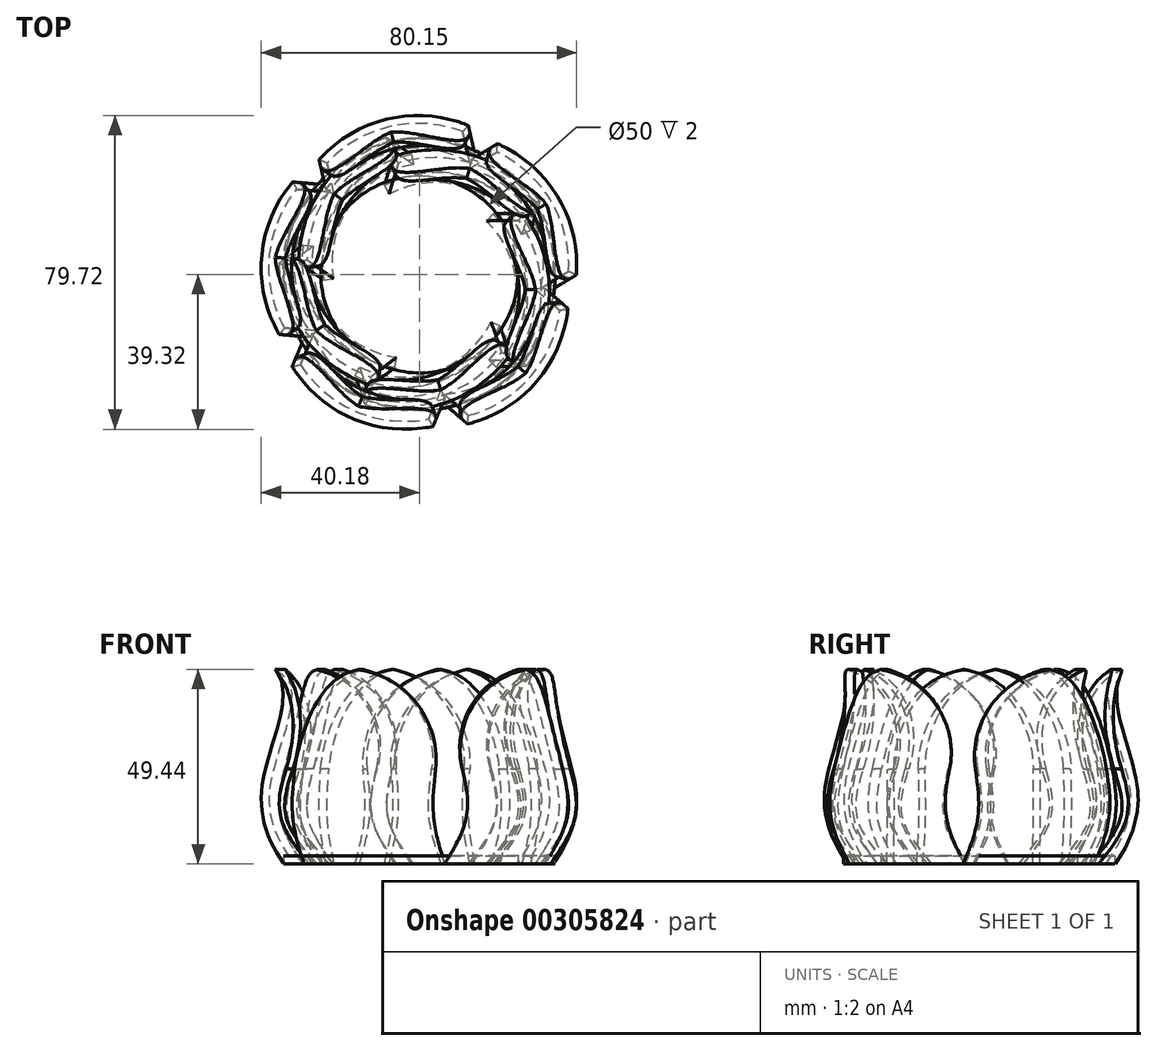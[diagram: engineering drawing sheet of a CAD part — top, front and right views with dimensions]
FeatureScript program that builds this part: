
annotation { "Feature Type Name" : "Feature", "Feature Type Description" : "" }
export const myFeature = defineFeature(function(context is Context, id is Id, definition is map)
    precondition{}
    {
        {
            var Q0;
            Q0=qCreatedBy(makeId("Top.planeOp"),FACE);
            var sketch = newSketch(context, id + "F0", { "sketchPlane" : qUnion([Q0])});
            skCircle(sketch, "E0", {"center": v(0, 0) * mm, "radius": 25 * mm});
            skSolve(sketch);
        }
        {
            var Q0;
            Q0=makeQuery(id+"F0.imprint","IMPRINT",FACE,{"disambiguationData":[TD([[makeQuery(id+"F0.imprint","IMPRINT",EDGE,{"derivedFrom":sQuery(id+"F0.wireOp",EDGE,"E0")}),1.0]])]});
            extrude(context, id + "F1", {"entities" : qUnion([Q0]), "depth" : 2 * mm});
        }
        {
            var Q0;
            Q0=qCreatedBy(makeId("Top.planeOp"),FACE);
            var sketch = newSketch(context, id + "F2", { "sketchPlane" : qUnion([Q0])});
            skArc(sketch, "E1.0", {"start": v(0, 25) * mm, "mid": v(-17.68, 17.68) * mm, "end": v(-25, 0) * mm});
            skArc(sketch, "E2.0", {"start": v(0, 27.5) * mm, "mid": v(-19.45, 19.45) * mm, "end": v(-27.5, 0) * mm});
            skLineSegment(sketch, "E3", {"start": v(0, 27.5) * mm, "end": v(0, 25) * mm});
            skLineSegment(sketch, "E4", {"start": v(-27.5, 0) * mm, "end": v(-25, 0) * mm});
            skSolve(sketch);
        }
        {
            var Q0;
            Q0=qCreatedBy(makeId("Right.planeOp"),FACE);
            var Q1;
            Q1=qCreatedBy(makeId("Front.planeOp"),FACE);
            cPlane(context, id + "F3", {"entities" : qUnion([Q0, Q1]), "cplaneType" : CPlaneType.MID_PLANE, "offset" : 25 * mm, "width" : 150 * mm, "height" : 150 * mm});
        }
        {
            var Q0;
            Q0=qCreatedBy(id+"F3.planeOp",FACE);
            var sketch = newSketch(context, id + "F4", { "sketchPlane" : qUnion([Q0])});
            skLineSegment(sketch, "E5.0", {"start": v(19.45, 0) * mm, "end": v(27.5, 0) * mm});
            skFitSpline(sketch, "E6", {"points": [v(27.5, 0) * mm, v(32.88, 21.22) * mm, v(30.27, 49.8) * mm], "startDerivative": vector(27.76, 40.4) * mm, "endDerivative": vector(35.36, 33.4) * mm});
            skSolve(sketch);
        }
        {
            var Q0;
            Q0=makeQuery(id+"F2.imprint","IMPRINT",FACE,{"disambiguationData":[TD([[makeQuery(id+"F2.imprint","IMPRINT",EDGE,{"derivedFrom":sQuery(id+"F2.wireOp",EDGE,"E1.0")}),-1.0]])]});
            var Q1;
            Q1=sQuery(id+"F4.wireOp",EDGE,"E6");
            sweep(context, id + "F5", {"profiles" : qUnion([Q0]), "path" : qUnion([Q1])});
        }
        {
            var Q0;
            Q0=qCreatedBy(id+"F3.planeOp",FACE);
            var sketch = newSketch(context, id + "F6", { "sketchPlane" : qUnion([Q0])});
            skLineSegment(sketch, "E7.0", {"start": v(-25, 2) * mm, "end": v(25, 2) * mm});
            skLineSegment(sketch, "E8", {"start": v(25, 2) * mm, "end": v(25, 51.54) * mm, "construction": true});
            skSolve(sketch);
        }
        {
            var Q0;
            Q0=makeQuery(id+"F5.opSweep","SWEPT_BODY",BODY,{"disambiguationData":[OSD([sQuery(id+"F2.wireOp",EDGE,"E1.0"),sQuery(id+"F2.wireOp",EDGE,"E2.0"),sQuery(id+"F2.wireOp",EDGE,"E3"),sQuery(id+"F2.wireOp",EDGE,"E4"),sQuery(id+"F4.wireOp",EDGE,"E6")])]});
            var Q1;
            Q1=sQuery(id+"F6.wireOp",EDGE,"E8");
            transform(context, id + "F7", {"entities" : qUnion([Q0]), "transformType" : TransformType.ROTATION, "transformAxis" : qUnion([Q1]), "angle" : 10 * degree, "makeCopy" : false});
        }
        {
            var Q0;
            Q0=makeQuery(id+"F5.opSweep","SWEPT_BODY",BODY,{"disambiguationData":[OSD([sQuery(id+"F2.wireOp",EDGE,"E1.0"),sQuery(id+"F2.wireOp",EDGE,"E2.0"),sQuery(id+"F2.wireOp",EDGE,"E3"),sQuery(id+"F2.wireOp",EDGE,"E4"),sQuery(id+"F4.wireOp",EDGE,"E6")])]});
            var Q1;
            Q1=makeQuery(id+"F1.opExtrude","CAP_EDGE",EDGE,{"disambiguationData":[OSD([sQuery(id+"F0.wireOp",EDGE,"E0")])],"isStart":false});
            circularPattern(context, id + "F8", {"entities" : qUnion([Q0]), "axis" : qUnion([Q1]), "angle" : 360 * degree, "instanceCount" : 5, "equalSpace" : true});
        }
        {
            var Q0;
            Q0=makeQuery(id+"F8.opPattern","COPY",BODY,{"derivedFrom":makeQuery(id+"F5.opSweep","SWEPT_BODY",BODY,{"disambiguationData":[OSD([sQuery(id+"F2.wireOp",EDGE,"E1.0"),sQuery(id+"F2.wireOp",EDGE,"E2.0"),sQuery(id+"F2.wireOp",EDGE,"E3"),sQuery(id+"F2.wireOp",EDGE,"E4"),sQuery(id+"F4.wireOp",EDGE,"E6")])]}),"instanceName":"4"});
            transform(context, id + "F9", {"entities" : qUnion([Q0]), "transformType" : TransformType.COPY});
        }
        {
            var Q0;
            Q0=makeQuery(id+"F9.opPattern","COPY",BODY,{"derivedFrom":makeQuery(id+"F8.opPattern","COPY",BODY,{"derivedFrom":makeQuery(id+"F5.opSweep","SWEPT_BODY",BODY,{"disambiguationData":[OSD([sQuery(id+"F2.wireOp",EDGE,"E1.0"),sQuery(id+"F2.wireOp",EDGE,"E2.0"),sQuery(id+"F2.wireOp",EDGE,"E3"),sQuery(id+"F2.wireOp",EDGE,"E4"),sQuery(id+"F4.wireOp",EDGE,"E6")])]}),"instanceName":"4"}),"instanceName":"1"});
            transform(context, id + "F10", {"entities" : qUnion([Q0]), "transformType" : TransformType.TRANSLATION_3D, "dx" : -14.4 * mm, "dy" : 8.9 * mm, "dz" : 0 * mm, "makeCopy" : false});
        }
        {
            var Q0;
            Q0=qCreatedBy(makeId("Right.planeOp"),FACE);
            var sketch = newSketch(context, id + "F11", { "sketchPlane" : qUnion([Q0])});
            skLineSegment(sketch, "E9", {"start": v(24.37, 0) * mm, "end": v(24.37, 62.17) * mm, "construction": true});
            skSolve(sketch);
        }
        {
            var Q0;
            Q0=makeQuery(id+"F9.opPattern","COPY",BODY,{"derivedFrom":makeQuery(id+"F8.opPattern","COPY",BODY,{"derivedFrom":makeQuery(id+"F5.opSweep","SWEPT_BODY",BODY,{"disambiguationData":[OSD([sQuery(id+"F2.wireOp",EDGE,"E1.0"),sQuery(id+"F2.wireOp",EDGE,"E2.0"),sQuery(id+"F2.wireOp",EDGE,"E3"),sQuery(id+"F2.wireOp",EDGE,"E4"),sQuery(id+"F4.wireOp",EDGE,"E6")])]}),"instanceName":"4"}),"instanceName":"1"});
            var Q1;
            Q1=sQuery(id+"F11.wireOp",EDGE,"E9");
            transform(context, id + "F12", {"entities" : qUnion([Q0]), "transformType" : TransformType.ROTATION, "transformAxis" : qUnion([Q1]), "angle" : 30 * degree, "makeCopy" : false});
        }
        {
            var Q0;
            Q0=makeQuery(id+"F9.opPattern","COPY",BODY,{"derivedFrom":makeQuery(id+"F8.opPattern","COPY",BODY,{"derivedFrom":makeQuery(id+"F5.opSweep","SWEPT_BODY",BODY,{"disambiguationData":[OSD([sQuery(id+"F2.wireOp",EDGE,"E1.0"),sQuery(id+"F2.wireOp",EDGE,"E2.0"),sQuery(id+"F2.wireOp",EDGE,"E3"),sQuery(id+"F2.wireOp",EDGE,"E4"),sQuery(id+"F4.wireOp",EDGE,"E6")])]}),"instanceName":"4"}),"instanceName":"1"});
            transform(context, id + "F13", {"entities" : qUnion([Q0]), "transformType" : TransformType.TRANSLATION_3D, "dx" : 0 * mm, "dy" : 2.7 * mm, "dz" : 0 * mm, "makeCopy" : false});
        }
        {
            var Q0;
            Q0=makeQuery(id+"F9.opPattern","COPY",BODY,{"derivedFrom":makeQuery(id+"F8.opPattern","COPY",BODY,{"derivedFrom":makeQuery(id+"F5.opSweep","SWEPT_BODY",BODY,{"disambiguationData":[OSD([sQuery(id+"F2.wireOp",EDGE,"E1.0"),sQuery(id+"F2.wireOp",EDGE,"E2.0"),sQuery(id+"F2.wireOp",EDGE,"E3"),sQuery(id+"F2.wireOp",EDGE,"E4"),sQuery(id+"F4.wireOp",EDGE,"E6")])]}),"instanceName":"4"}),"instanceName":"1"});
            var Q1;
            Q1=makeQuery(id+"F1.opExtrude","CAP_EDGE",EDGE,{"disambiguationData":[OSD([sQuery(id+"F0.wireOp",EDGE,"E0")])],"isStart":false});
            circularPattern(context, id + "F14", {"entities" : qUnion([Q0]), "axis" : qUnion([Q1]), "angle" : 360 * degree, "instanceCount" : 5, "equalSpace" : true});
        }
        {
            var Q0;
            Q0=makeQuery(id+"F8.opPattern","COPY",EDGE,{"derivedFrom":makeQuery(id+"F5.opSweep","CAP_EDGE",EDGE,{"disambiguationData":[OSD([sQuery(id+"F2.wireOp",EDGE,"E4"),sQuery(id+"F4.wireOp",VERTEX,"E6.end")])],"isStart":false}),"instanceName":"1"});
            var Q1;
            Q1=makeQuery(id+"F8.opPattern","COPY",EDGE,{"derivedFrom":makeQuery(id+"F5.opSweep","CAP_EDGE",EDGE,{"disambiguationData":[OSD([sQuery(id+"F2.wireOp",EDGE,"E3"),sQuery(id+"F4.wireOp",VERTEX,"E6.end")])],"isStart":false}),"instanceName":"1"});
            var Q2;
            Q2=makeQuery(id+"F5.opSweep","CAP_EDGE",EDGE,{"disambiguationData":[OSD([sQuery(id+"F2.wireOp",EDGE,"E4"),sQuery(id+"F4.wireOp",VERTEX,"E6.end")])],"isStart":false});
            var Q3;
            Q3=makeQuery(id+"F5.opSweep","CAP_EDGE",EDGE,{"disambiguationData":[OSD([sQuery(id+"F2.wireOp",EDGE,"E3"),sQuery(id+"F4.wireOp",VERTEX,"E6.end")])],"isStart":false});
            var Q4;
            Q4=makeQuery(id+"F8.opPattern","COPY",EDGE,{"derivedFrom":makeQuery(id+"F5.opSweep","CAP_EDGE",EDGE,{"disambiguationData":[OSD([sQuery(id+"F2.wireOp",EDGE,"E4"),sQuery(id+"F4.wireOp",VERTEX,"E6.end")])],"isStart":false}),"instanceName":"4"});
            var Q5;
            Q5=makeQuery(id+"F9.opPattern","COPY",EDGE,{"derivedFrom":makeQuery(id+"F8.opPattern","COPY",EDGE,{"derivedFrom":makeQuery(id+"F5.opSweep","CAP_EDGE",EDGE,{"disambiguationData":[OSD([sQuery(id+"F2.wireOp",EDGE,"E4"),sQuery(id+"F4.wireOp",VERTEX,"E6.end")])],"isStart":false}),"instanceName":"4"}),"instanceName":"1"});
            var Q6;
            Q6=makeQuery(id+"F14.opPattern","COPY",EDGE,{"derivedFrom":makeQuery(id+"F9.opPattern","COPY",EDGE,{"derivedFrom":makeQuery(id+"F8.opPattern","COPY",EDGE,{"derivedFrom":makeQuery(id+"F5.opSweep","CAP_EDGE",EDGE,{"disambiguationData":[OSD([sQuery(id+"F2.wireOp",EDGE,"E3"),sQuery(id+"F4.wireOp",VERTEX,"E6.end")])],"isStart":false}),"instanceName":"4"}),"instanceName":"1"}),"instanceName":"1"});
            var Q7;
            Q7=makeQuery(id+"F9.opPattern","COPY",EDGE,{"derivedFrom":makeQuery(id+"F8.opPattern","COPY",EDGE,{"derivedFrom":makeQuery(id+"F5.opSweep","CAP_EDGE",EDGE,{"disambiguationData":[OSD([sQuery(id+"F2.wireOp",EDGE,"E3"),sQuery(id+"F4.wireOp",VERTEX,"E6.end")])],"isStart":false}),"instanceName":"4"}),"instanceName":"1"});
            var Q8;
            Q8=makeQuery(id+"F14.opPattern","COPY",EDGE,{"derivedFrom":makeQuery(id+"F9.opPattern","COPY",EDGE,{"derivedFrom":makeQuery(id+"F8.opPattern","COPY",EDGE,{"derivedFrom":makeQuery(id+"F5.opSweep","CAP_EDGE",EDGE,{"disambiguationData":[OSD([sQuery(id+"F2.wireOp",EDGE,"E4"),sQuery(id+"F4.wireOp",VERTEX,"E6.end")])],"isStart":false}),"instanceName":"4"}),"instanceName":"1"}),"instanceName":"4"});
            var Q9;
            Q9=makeQuery(id+"F8.opPattern","COPY",EDGE,{"derivedFrom":makeQuery(id+"F5.opSweep","CAP_EDGE",EDGE,{"disambiguationData":[OSD([sQuery(id+"F2.wireOp",EDGE,"E3"),sQuery(id+"F4.wireOp",VERTEX,"E6.end")])],"isStart":false}),"instanceName":"4"});
            var Q10;
            Q10=makeQuery(id+"F8.opPattern","COPY",EDGE,{"derivedFrom":makeQuery(id+"F5.opSweep","CAP_EDGE",EDGE,{"disambiguationData":[OSD([sQuery(id+"F2.wireOp",EDGE,"E4"),sQuery(id+"F4.wireOp",VERTEX,"E6.end")])],"isStart":false}),"instanceName":"3"});
            var Q11;
            Q11=makeQuery(id+"F14.opPattern","COPY",EDGE,{"derivedFrom":makeQuery(id+"F9.opPattern","COPY",EDGE,{"derivedFrom":makeQuery(id+"F8.opPattern","COPY",EDGE,{"derivedFrom":makeQuery(id+"F5.opSweep","CAP_EDGE",EDGE,{"disambiguationData":[OSD([sQuery(id+"F2.wireOp",EDGE,"E3"),sQuery(id+"F4.wireOp",VERTEX,"E6.end")])],"isStart":false}),"instanceName":"4"}),"instanceName":"1"}),"instanceName":"4"});
            var Q12;
            Q12=makeQuery(id+"F14.opPattern","COPY",EDGE,{"derivedFrom":makeQuery(id+"F9.opPattern","COPY",EDGE,{"derivedFrom":makeQuery(id+"F8.opPattern","COPY",EDGE,{"derivedFrom":makeQuery(id+"F5.opSweep","CAP_EDGE",EDGE,{"disambiguationData":[OSD([sQuery(id+"F2.wireOp",EDGE,"E4"),sQuery(id+"F4.wireOp",VERTEX,"E6.end")])],"isStart":false}),"instanceName":"4"}),"instanceName":"1"}),"instanceName":"3"});
            var Q13;
            Q13=makeQuery(id+"F8.opPattern","COPY",EDGE,{"derivedFrom":makeQuery(id+"F5.opSweep","CAP_EDGE",EDGE,{"disambiguationData":[OSD([sQuery(id+"F2.wireOp",EDGE,"E3"),sQuery(id+"F4.wireOp",VERTEX,"E6.end")])],"isStart":false}),"instanceName":"3"});
            var Q14;
            Q14=makeQuery(id+"F8.opPattern","COPY",EDGE,{"derivedFrom":makeQuery(id+"F5.opSweep","CAP_EDGE",EDGE,{"disambiguationData":[OSD([sQuery(id+"F2.wireOp",EDGE,"E4"),sQuery(id+"F4.wireOp",VERTEX,"E6.end")])],"isStart":false}),"instanceName":"2"});
            var Q15;
            Q15=makeQuery(id+"F14.opPattern","COPY",EDGE,{"derivedFrom":makeQuery(id+"F9.opPattern","COPY",EDGE,{"derivedFrom":makeQuery(id+"F8.opPattern","COPY",EDGE,{"derivedFrom":makeQuery(id+"F5.opSweep","CAP_EDGE",EDGE,{"disambiguationData":[OSD([sQuery(id+"F2.wireOp",EDGE,"E3"),sQuery(id+"F4.wireOp",VERTEX,"E6.end")])],"isStart":false}),"instanceName":"4"}),"instanceName":"1"}),"instanceName":"3"});
            var Q16;
            Q16=makeQuery(id+"F14.opPattern","COPY",EDGE,{"derivedFrom":makeQuery(id+"F9.opPattern","COPY",EDGE,{"derivedFrom":makeQuery(id+"F8.opPattern","COPY",EDGE,{"derivedFrom":makeQuery(id+"F5.opSweep","CAP_EDGE",EDGE,{"disambiguationData":[OSD([sQuery(id+"F2.wireOp",EDGE,"E4"),sQuery(id+"F4.wireOp",VERTEX,"E6.end")])],"isStart":false}),"instanceName":"4"}),"instanceName":"1"}),"instanceName":"2"});
            var Q17;
            Q17=makeQuery(id+"F8.opPattern","COPY",EDGE,{"derivedFrom":makeQuery(id+"F5.opSweep","CAP_EDGE",EDGE,{"disambiguationData":[OSD([sQuery(id+"F2.wireOp",EDGE,"E3"),sQuery(id+"F4.wireOp",VERTEX,"E6.end")])],"isStart":false}),"instanceName":"2"});
            var Q18;
            Q18=makeQuery(id+"F14.opPattern","COPY",EDGE,{"derivedFrom":makeQuery(id+"F9.opPattern","COPY",EDGE,{"derivedFrom":makeQuery(id+"F8.opPattern","COPY",EDGE,{"derivedFrom":makeQuery(id+"F5.opSweep","CAP_EDGE",EDGE,{"disambiguationData":[OSD([sQuery(id+"F2.wireOp",EDGE,"E3"),sQuery(id+"F4.wireOp",VERTEX,"E6.end")])],"isStart":false}),"instanceName":"4"}),"instanceName":"1"}),"instanceName":"2"});
            var Q19;
            Q19=makeQuery(id+"F14.opPattern","COPY",EDGE,{"derivedFrom":makeQuery(id+"F9.opPattern","COPY",EDGE,{"derivedFrom":makeQuery(id+"F8.opPattern","COPY",EDGE,{"derivedFrom":makeQuery(id+"F5.opSweep","CAP_EDGE",EDGE,{"disambiguationData":[OSD([sQuery(id+"F2.wireOp",EDGE,"E4"),sQuery(id+"F4.wireOp",VERTEX,"E6.end")])],"isStart":false}),"instanceName":"4"}),"instanceName":"1"}),"instanceName":"1"});
            fillet(context, id + "F15", {"entities" : qUnion([Q0, Q1, Q2, Q3, Q4, Q5, Q6, Q7, Q8, Q9, Q10, Q11, Q12, Q13, Q14, Q15, Q16, Q17, Q18, Q19]), "radius" : 19 * mm, "tangentPropagation" : true, "allowEdgeOverflow" : false});
        }
        {
            var Q0;
            Q0=qCreatedBy(makeId("Top.planeOp"),FACE);
            var sketch = newSketch(context, id + "F16", { "sketchPlane" : qUnion([Q0])});
            skCircle(sketch, "E10.0", {"center": v(0, 0) * mm, "radius": 25 * mm});
            skCircle(sketch, "E11.0", {"center": v(0, 0) * mm, "radius": 34.5 * mm});
            skSolve(sketch);
        }
        {
            var Q0;
            Q0=makeQuery(id+"F16.imprint","IMPRINT",FACE,{"disambiguationData":[TD([[makeQuery(id+"F16.imprint","IMPRINT",EDGE,{"derivedFrom":sQuery(id+"F16.wireOp",EDGE,"E10.0")}),-1.0]])]});
            extrude(context, id + "F17", {"entities" : qUnion([Q0]), "depth" : 2 * mm});
        }
    });
